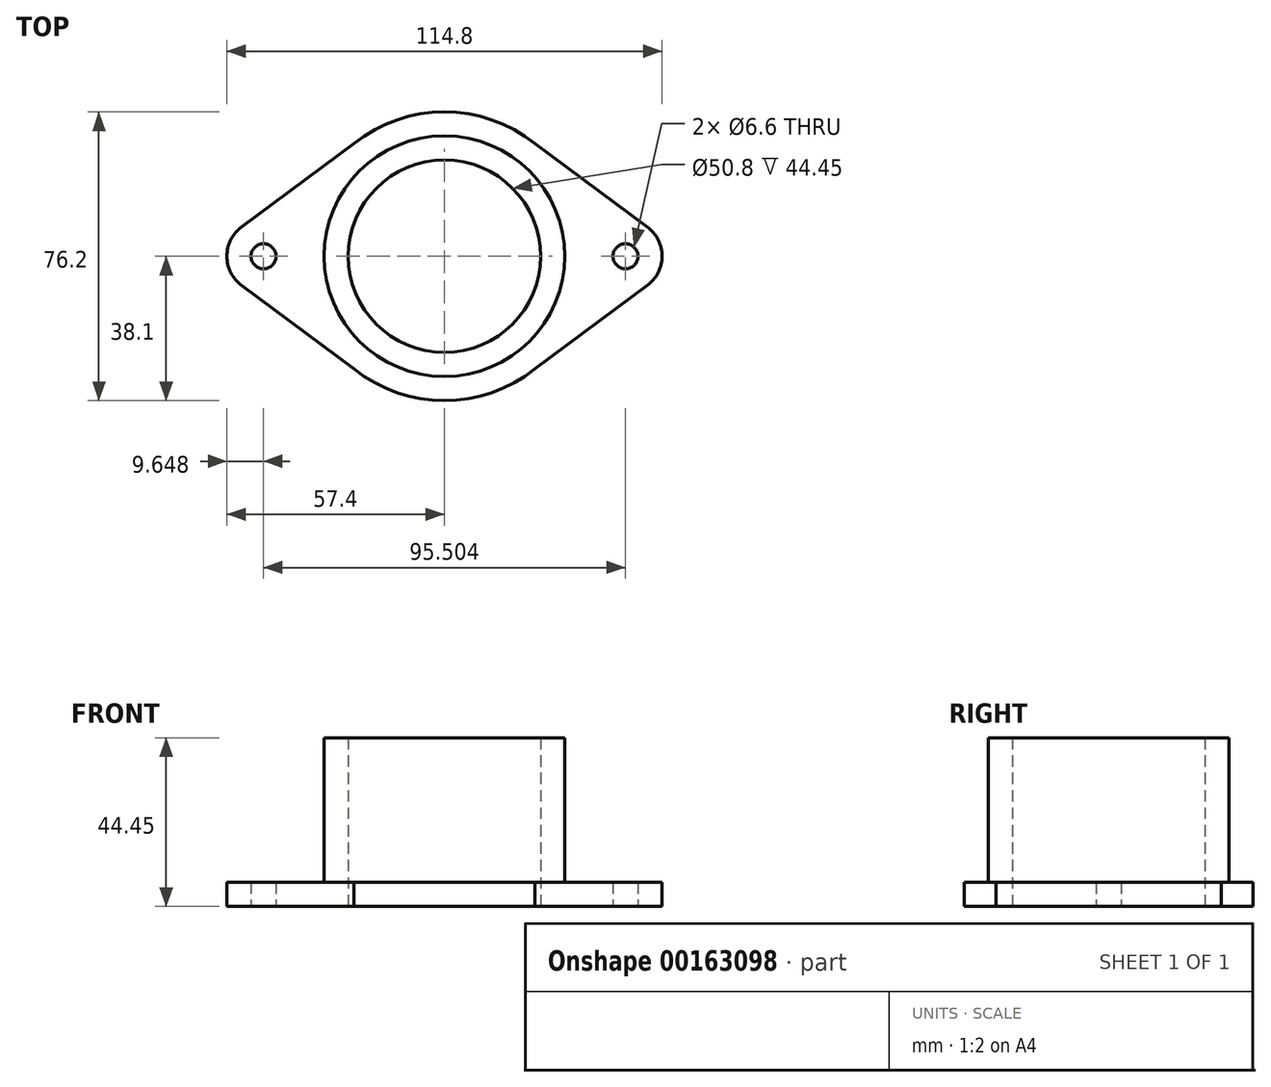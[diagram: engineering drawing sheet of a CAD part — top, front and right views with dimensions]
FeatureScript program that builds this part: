
annotation { "Feature Type Name" : "Feature", "Feature Type Description" : "" }
export const myFeature = defineFeature(function(context is Context, id is Id, definition is map)
    precondition{}
    {
        {
            var Q0;
            Q0=qCreatedBy(makeId("Top.planeOp"),FACE);
            var sketch = newSketch(context, id + "F0", { "sketchPlane" : qUnion([Q0])});
            skArc(sketch, "E0", {"start": v(-23.83, -29.73) * mm, "mid": v(0, -38.1) * mm, "end": v(23.83, -29.73) * mm});
            skCircle(sketch, "E1", {"center": v(0, 0) * mm, "radius": 31.75 * mm});
            skCircle(sketch, "E2", {"center": v(-47.75, 0) * mm, "radius": 3.3 * mm});
            skCircle(sketch, "E3", {"center": v(47.75, 0) * mm, "radius": 3.3 * mm});
            skArc(sketch, "E4", {"start": v(53.5, -7.76) * mm, "mid": v(57.4, 0) * mm, "end": v(53.5, 7.76) * mm});
            skArc(sketch, "E5", {"start": v(-53.5, 7.76) * mm, "mid": v(-57.4, 0) * mm, "end": v(-53.5, -7.76) * mm});
            skLineSegment(sketch, "E6", {"start": v(-53.5, 7.76) * mm, "end": v(-23.83, 29.73) * mm});
            skLineSegment(sketch, "E7", {"start": v(-23.83, -29.73) * mm, "end": v(-53.5, -7.76) * mm});
            skLineSegment(sketch, "E8", {"start": v(23.83, -29.73) * mm, "end": v(53.5, -7.76) * mm});
            skLineSegment(sketch, "E9", {"start": v(53.5, 7.76) * mm, "end": v(23.83, 29.73) * mm});
            skArc(sketch, "E10.trimOffspring", {"start": v(23.83, 29.73) * mm, "mid": v(0, 38.1) * mm, "end": v(-23.83, 29.73) * mm});
            skSolve(sketch);
        }
        {
            var Q0;
            Q0=makeQuery(id+"F0.imprint","IMPRINT",FACE,{"disambiguationData":[TD([[makeQuery(id+"F0.imprint","IMPRINT",EDGE,{"derivedFrom":sQuery(id+"F0.wireOp",EDGE,"E0")}),1.0]])]});
            extrude(context, id + "F1", {"entities" : qUnion([Q0]), "depth" : 6.35 * mm});
        }
        {
            var Q0;
            Q0=qCreatedBy(makeId("Top.planeOp"),FACE);
            var sketch = newSketch(context, id + "F2", { "sketchPlane" : qUnion([Q0])});
            skCircle(sketch, "E11", {"center": v(0, 0) * mm, "radius": 25.4 * mm});
            skCircle(sketch, "E12", {"center": v(0, 0) * mm, "radius": 31.75 * mm});
            skSolve(sketch);
        }
        {
            var Q0;
            Q0=makeQuery(id+"F2.imprint","IMPRINT",FACE,{"disambiguationData":[TD([[makeQuery(id+"F2.imprint","IMPRINT",EDGE,{"derivedFrom":sQuery(id+"F2.wireOp",EDGE,"E11")}),-1.0]])]});
            extrude(context, id + "F3", {"entities" : qUnion([Q0]), "operationType" : NewBodyOperationType.ADD, "depth" : 44.45 * mm});
        }
    });
